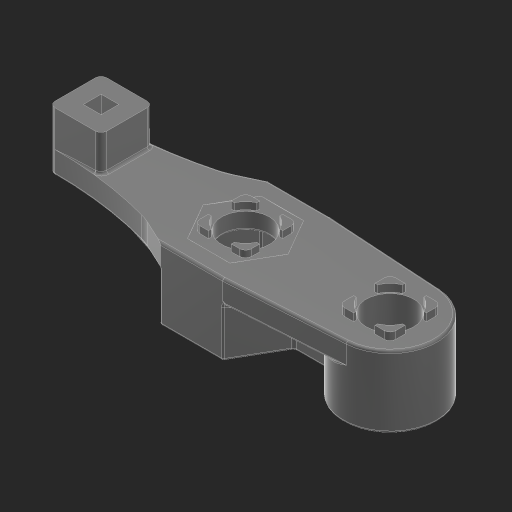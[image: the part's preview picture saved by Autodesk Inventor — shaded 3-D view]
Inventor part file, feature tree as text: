
AUTODESK INVENTOR PART (.ipt)
format: ipt  version: 2023 (Build 270158000, 158)  size: 457,728 bytes
history: native  units: in
note: dims shown in document units (in); Inventor stores cm internally (conversion verified against a paired STEP export)
features: fillet x1
ambient origin geometry x8: Origin, YZ Plane, XZ Plane, XY Plane, X Axis, Y Axis, Z Axis, Center Point
bodies: Solid1 (feature_tree)
feature tree (1):
  fillet  "Fillet18"  [1 undecoded]
note: 1 required parameter value undecoded (feature->parameter linkage not recoverable at this tier; creation-order binding heuristic only, values carry confidence <= 0.55)
